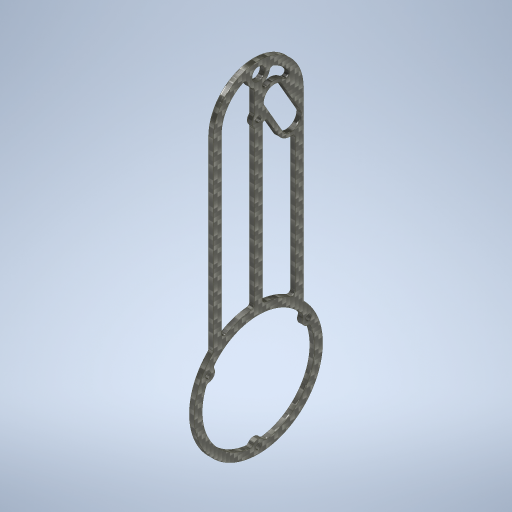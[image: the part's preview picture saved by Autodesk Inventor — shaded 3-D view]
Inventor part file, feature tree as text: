
AUTODESK INVENTOR PART (.ipt)
format: ipt  version: 2024.2 (Build 282272000, 272)  size: 499,712 bytes
history: native  units: mm
features: hole x2, sketch x1, extrude x1
ambient origin geometry x8: Origin, YZ Plane, XZ Plane, XY Plane, X Axis, Y Axis, Z Axis, Center Point
bodies: Solid1 (feature_tree)
feature tree (4):
  sketch  "Sketch1"  dims[d1=205.0mm d2=80.0mm d3=8.0mm d5=8.1mm d6=3.0mm d7=0.0mm d8=8.0mm d9=6.0mm d10=4.0mm d11=2.0mm d12=90.0deg d13=8.1mm d14=0.0mm d15=8.8mm d16=12.5mm d17=10.0mm d18=1.85mm d19=1.85mm d20=60.0deg d21=20.0mm d22=20.0mm d24=20.0mm d29=30.0deg d30=8.0mm d31=72.0mm d32=120.0deg d33=3.5mm d34=6.0mm d35=4.0mm d36=2.0mm d37=90.0deg d38=6.0mm d39=0.0mm d40=7.0mm d41=56.0mm d42=2.0mm d43=24.5mm d44=5.0mm d45=5.0mm d46=5.0mm d48=3.15mm d50=8.0mm d52=2.0mm d54=5.0mm d57=9.0mm d58=8.0mm]
  extrude  "Extrusion1"  Depth=9.0mm
  hole  "Phi8.0-H7"  [1 undecoded]
  hole  "Phi3.5"  [1 undecoded]
note: 2 required parameter values undecoded (feature->parameter linkage not recoverable at this tier; creation-order binding heuristic only, values carry confidence <= 0.55)
